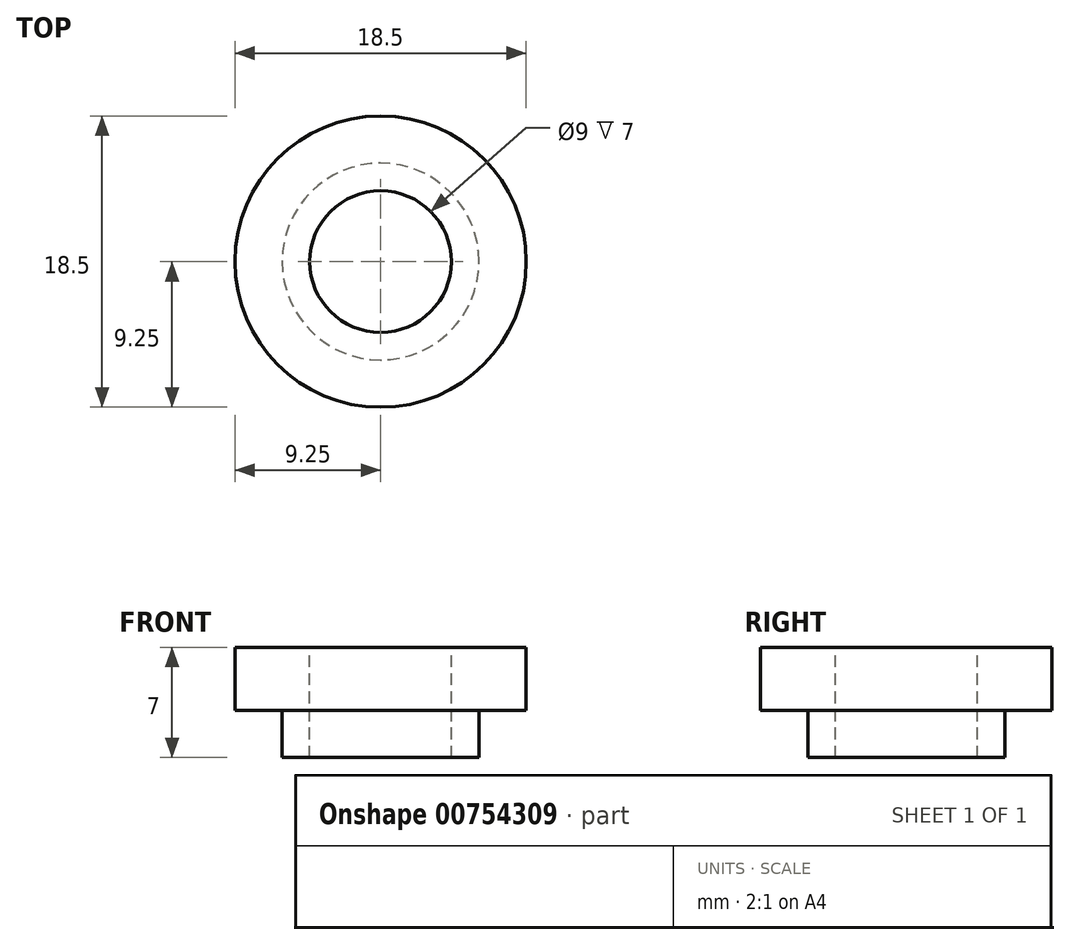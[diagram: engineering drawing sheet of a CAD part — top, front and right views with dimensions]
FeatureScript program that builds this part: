
annotation { "Feature Type Name" : "Feature", "Feature Type Description" : "" }
export const myFeature = defineFeature(function(context is Context, id is Id, definition is map)
    precondition{}
    {
        {
            var Q0;
            Q0=qCreatedBy(makeId("Top.planeOp"),FACE);
            var sketch = newSketch(context, id + "F0", { "sketchPlane" : qUnion([Q0])});
            skCircle(sketch, "E0", {"center": v(0, 0) * mm, "radius": 6.25 * mm});
            skCircle(sketch, "E1", {"center": v(0, 0) * mm, "radius": 9.25 * mm});
            skCircle(sketch, "E2", {"center": v(0, 0) * mm, "radius": 4.5 * mm});
            skSolve(sketch);
        }
        {
            var Q0;
            Q0=makeQuery(id+"F0.imprint","IMPRINT",FACE,{"disambiguationData":[TD([[makeQuery(id+"F0.imprint","IMPRINT",EDGE,{"derivedFrom":sQuery(id+"F0.wireOp",EDGE,"E0")}),1.0]])]});
            extrude(context, id + "F1", {"entities" : qUnion([Q0]), "oppositeDirection" : true, "depth" : 3 * mm, "offsetDistance" : 25 * mm, "hasSecondDirection" : true, "secondDirectionOppositeDirection" : false, "secondDirectionDepth" : 4 * mm});
        }
        {
            var Q0;
            Q0=makeQuery(id+"F0.imprint","IMPRINT",FACE,{"disambiguationData":[TD([[makeQuery(id+"F0.imprint","IMPRINT",EDGE,{"derivedFrom":sQuery(id+"F0.wireOp",EDGE,"E0")}),-1.0]])]});
            extrude(context, id + "F2", {"entities" : qUnion([Q0]), "operationType" : NewBodyOperationType.ADD, "depth" : 4 * mm, "offsetDistance" : 25 * mm});
        }
    });
